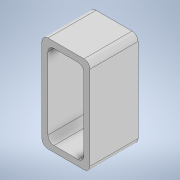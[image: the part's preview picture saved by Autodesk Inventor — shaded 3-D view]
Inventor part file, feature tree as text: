
AUTODESK INVENTOR PART (.ipt)
format: ipt  version: 2020 (Build 240168000, 168)  size: 117,760 bytes
history: native  units: in
note: dims shown in document units (in); Inventor stores cm internally (conversion verified against a paired STEP export)
features: extrude x1, sketch x1
ambient origin geometry x8: Origin, YZ Plane, XZ Plane, XY Plane, X Axis, Y Axis, Z Axis, Center Point
bodies: Solid1 (feature_tree)
feature tree (2):
  extrude  "Extrusion1"  Depth=1.0in
  sketch  "Sketch1"  dims[d0=2.0in d1=1.0in d2=0.125in d3=0.125in d4=0.125in d5=0.125in d6=0.125in d7=0.125in d8=0.125in d9=0.125in d10=0.125in d11=1.0in d12=0.0in]
